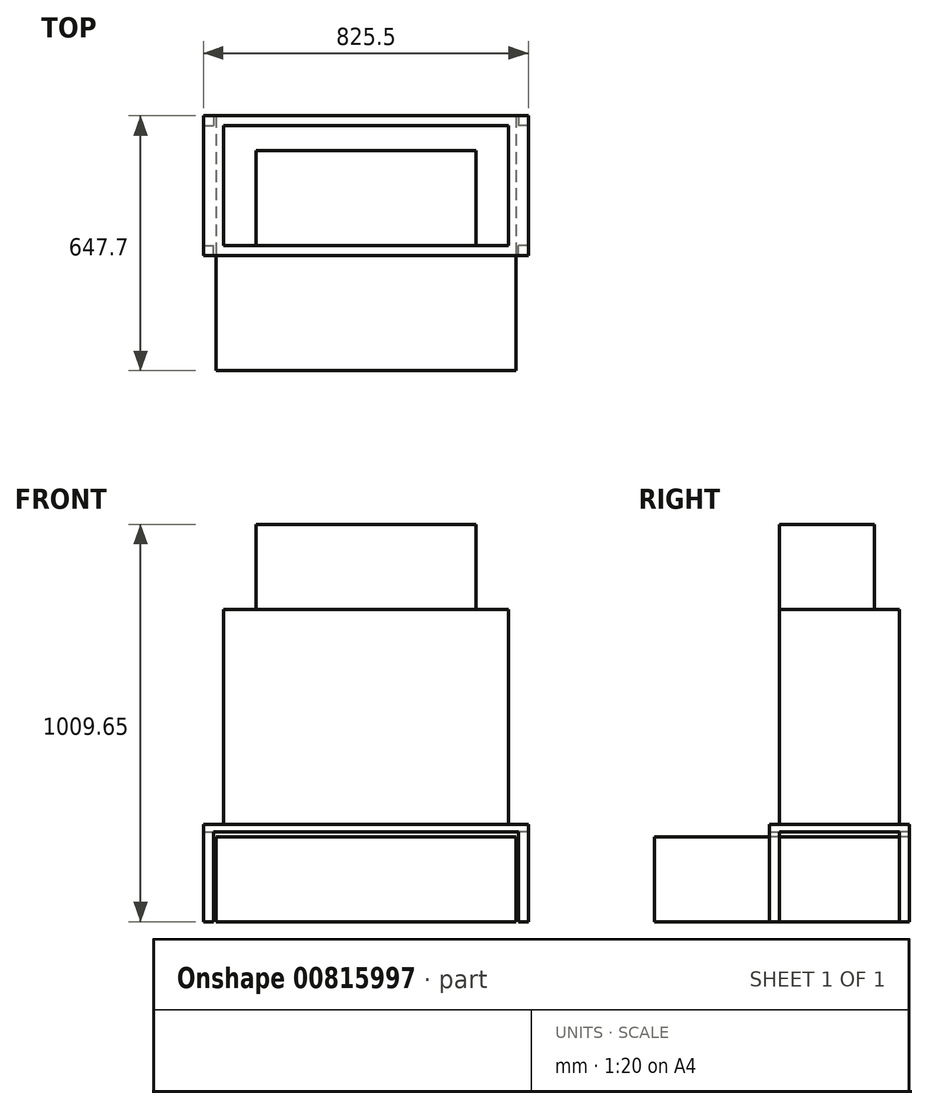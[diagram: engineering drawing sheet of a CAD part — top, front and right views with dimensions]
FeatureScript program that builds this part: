
annotation { "Feature Type Name" : "Feature", "Feature Type Description" : "" }
export const myFeature = defineFeature(function(context is Context, id is Id, definition is map)
    precondition{}
    {
        {
            var Q0;
            Q0=qCreatedBy(makeId("Top.planeOp"),FACE);
            var sketch = newSketch(context, id + "F0", { "sketchPlane" : qUnion([Q0])});
            skLineSegment(sketch, "E0.bottom", {"start": v(361.95, 152.4) * mm, "end": v(-361.95, 152.4) * mm});
            skLineSegment(sketch, "E0.top", {"start": v(361.95, -152.4) * mm, "end": v(-361.95, -152.4) * mm});
            skLineSegment(sketch, "E0.left", {"start": v(361.95, 152.4) * mm, "end": v(361.95, -152.4) * mm});
            skLineSegment(sketch, "E0.right", {"start": v(-361.95, 152.4) * mm, "end": v(-361.95, -152.4) * mm});
            skPoint(sketch, "E0.middle", {"position": v(0, 0) * mm});
            skSolve(sketch);
        }
        {
            var Q0;
            Q0 = qSketchRegion(id + "F0", true);
            extrude(context, id + "F1", {"entities" : qUnion([Q0]), "depth" : 546.1 * mm, "offsetDistance" : 25.4 * mm});
        }
        {
            var Q0;
            Q0=makeQuery(id+"F1.opExtrude","CAP_FACE",FACE,{"disambiguationData":[OSD([sQuery(id+"F0.wireOp",EDGE,"E0.bottom"),sQuery(id+"F0.wireOp",EDGE,"E0.top"),sQuery(id+"F0.wireOp",EDGE,"E0.left"),sQuery(id+"F0.wireOp",EDGE,"E0.right")])],"isStart":false});
            var sketch = newSketch(context, id + "F2", { "sketchPlane" : qUnion([Q0])});
            skLineSegment(sketch, "E1.bottom", {"start": v(-279.4, -152.4) * mm, "end": v(279.4, -152.4) * mm});
            skLineSegment(sketch, "E1.top", {"start": v(-279.4, 88.9) * mm, "end": v(279.4, 88.9) * mm});
            skLineSegment(sketch, "E1.left", {"start": v(-279.4, -152.4) * mm, "end": v(-279.4, 88.9) * mm});
            skLineSegment(sketch, "E1.right", {"start": v(279.4, -152.4) * mm, "end": v(279.4, 88.9) * mm});
            skLineSegment(sketch, "E2", {"start": v(0, 88.9) * mm, "end": v(0, 152.4) * mm, "construction": true});
            skSolve(sketch);
        }
        {
            var Q0;
            Q0 = qSketchRegion(id + "F2", true);
            extrude(context, id + "F3", {"entities" : qUnion([Q0]), "depth" : 215.9 * mm, "offsetDistance" : 25.4 * mm});
        }
        {
            var Q0;
            Q0=makeQuery(id+"F1.opExtrude","CAP_FACE",FACE,{"disambiguationData":[OSD([sQuery(id+"F0.wireOp",EDGE,"E0.bottom"),sQuery(id+"F0.wireOp",EDGE,"E0.top"),sQuery(id+"F0.wireOp",EDGE,"E0.left"),sQuery(id+"F0.wireOp",EDGE,"E0.right")])],"isStart":true});
            var sketch = newSketch(context, id + "F4", { "sketchPlane" : qUnion([Q0])});
            skLineSegment(sketch, "E3.bottom", {"start": v(-412.75, 177.8) * mm, "end": v(412.75, 177.8) * mm});
            skLineSegment(sketch, "E3.top", {"start": v(-412.75, -177.8) * mm, "end": v(412.75, -177.8) * mm});
            skLineSegment(sketch, "E3.left", {"start": v(-412.75, 177.8) * mm, "end": v(-412.75, -177.8) * mm});
            skLineSegment(sketch, "E3.right", {"start": v(412.75, 177.8) * mm, "end": v(412.75, -177.8) * mm});
            skPoint(sketch, "E3.middle", {"position": v(0, 0) * mm});
            skSolve(sketch);
        }
        {
            var Q0;
            Q0 = qSketchRegion(id + "F4", true);
            extrude(context, id + "F5", {"entities" : qUnion([Q0]), "depth" : 19.05 * mm, "offsetDistance" : 25.4 * mm});
        }
        {
            var Q0;
            Q0=makeQuery(id+"F5.opExtrude","CAP_FACE",FACE,{"disambiguationData":[OSD([sQuery(id+"F4.wireOp",EDGE,"E3.bottom"),sQuery(id+"F4.wireOp",EDGE,"E3.top"),sQuery(id+"F4.wireOp",EDGE,"E3.left"),sQuery(id+"F4.wireOp",EDGE,"E3.right")])],"isStart":false});
            var sketch = newSketch(context, id + "F6", { "sketchPlane" : qUnion([Q0])});
            skLineSegment(sketch, "E4.bottom", {"start": v(-412.75, 177.8) * mm, "end": v(-387.35, 177.8) * mm});
            skLineSegment(sketch, "E4.top", {"start": v(-412.75, 152.4) * mm, "end": v(-387.35, 152.4) * mm});
            skLineSegment(sketch, "E4.left", {"start": v(-412.75, 177.8) * mm, "end": v(-412.75, 152.4) * mm});
            skLineSegment(sketch, "E4.right", {"start": v(-387.35, 177.8) * mm, "end": v(-387.35, 152.4) * mm});
            skLineSegment(sketch, "E5.bottom", {"start": v(-412.75, -177.8) * mm, "end": v(-387.35, -177.8) * mm});
            skLineSegment(sketch, "E5.top", {"start": v(-412.75, -152.4) * mm, "end": v(-387.35, -152.4) * mm});
            skLineSegment(sketch, "E5.left", {"start": v(-412.75, -177.8) * mm, "end": v(-412.75, -152.4) * mm});
            skLineSegment(sketch, "E5.right", {"start": v(-387.35, -177.8) * mm, "end": v(-387.35, -152.4) * mm});
            skLineSegment(sketch, "E6.bottom", {"start": v(412.75, -177.8) * mm, "end": v(387.35, -177.8) * mm});
            skLineSegment(sketch, "E6.top", {"start": v(412.75, -152.4) * mm, "end": v(387.35, -152.4) * mm});
            skLineSegment(sketch, "E6.left", {"start": v(412.75, -177.8) * mm, "end": v(412.75, -152.4) * mm});
            skLineSegment(sketch, "E6.right", {"start": v(387.35, -177.8) * mm, "end": v(387.35, -152.4) * mm});
            skLineSegment(sketch, "E7.bottom", {"start": v(412.75, 177.8) * mm, "end": v(387.35, 177.8) * mm});
            skLineSegment(sketch, "E7.top", {"start": v(412.75, 152.4) * mm, "end": v(387.35, 152.4) * mm});
            skLineSegment(sketch, "E7.left", {"start": v(412.75, 177.8) * mm, "end": v(412.75, 152.4) * mm});
            skLineSegment(sketch, "E7.right", {"start": v(387.35, 177.8) * mm, "end": v(387.35, 152.4) * mm});
            skSolve(sketch);
        }
        {
            var Q0;
            Q0 = qSketchRegion(id + "F6", true);
            extrude(context, id + "F7", {"entities" : qUnion([Q0]), "operationType" : NewBodyOperationType.ADD, "depth" : 228.6 * mm, "offsetDistance" : 25.4 * mm});
        }
        {
            var Q0;
            Q0=makeQuery(id+"F7.opExtrude","CAP_FACE",FACE,{"disambiguationData":[OSD([sQuery(id+"F6.wireOp",EDGE,"E5.bottom"),sQuery(id+"F6.wireOp",EDGE,"E5.top"),sQuery(id+"F6.wireOp",EDGE,"E5.left"),sQuery(id+"F6.wireOp",EDGE,"E5.right")])],"isStart":false});
            var sketch = newSketch(context, id + "F8", { "sketchPlane" : qUnion([Q0])});
            skLineSegment(sketch, "E8.bottom", {"start": v(-381, -177.8) * mm, "end": v(381, -177.8) * mm});
            skLineSegment(sketch, "E8.top", {"start": v(-381, 469.9) * mm, "end": v(381, 469.9) * mm});
            skLineSegment(sketch, "E8.left", {"start": v(-381, -177.8) * mm, "end": v(-381, 469.9) * mm});
            skLineSegment(sketch, "E8.right", {"start": v(381, -177.8) * mm, "end": v(381, 469.9) * mm});
            skSolve(sketch);
        }
        {
            var Q0;
            Q0=makeQuery(id+"F8.imprint","IMPRINT",FACE,{"disambiguationData":[TD([[makeQuery(id+"F8.imprint","IMPRINT",EDGE,{"derivedFrom":sQuery(id+"F8.wireOp",EDGE,"E8.bottom")}),1.0]])]});
            extrude(context, id + "F9", {"entities" : qUnion([Q0]), "oppositeDirection" : true, "depth" : 215.9 * mm, "offsetDistance" : 25.4 * mm});
        }
    });
